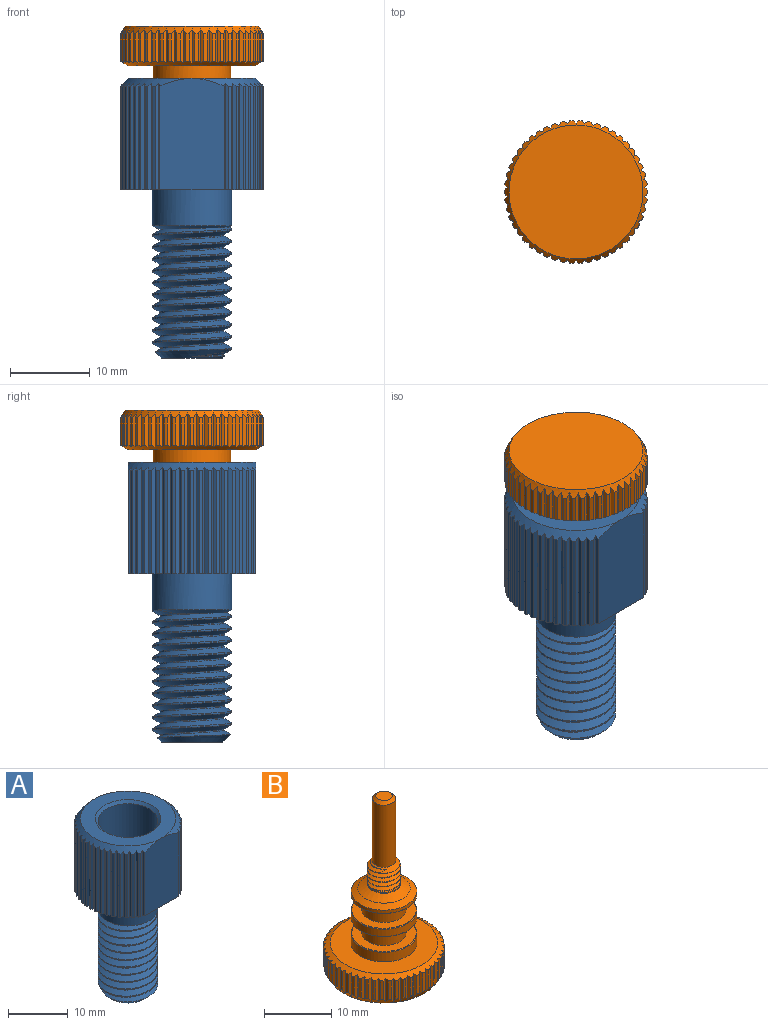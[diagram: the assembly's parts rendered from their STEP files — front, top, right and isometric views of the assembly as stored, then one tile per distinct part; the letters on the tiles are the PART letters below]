
ASSEMBLY  parts=2 mates=1
PART A: 163 faces, bbox 18.3x18.3x36.1 mm
  f0: plane 6.91x6.91mm, normal (0,0,-1), area 7.4mm2, adj f68,f74,f159,f160,f161
  f1: cone r=8mm half-angle=45deg, axis (0,0,-1), area 26.7mm2, adj f21,f22,f23,f24,f25,f26,f27,f28
  f2: plane 18x16mm, normal (0,0,-1), area 59.2mm2, adj f4,f5,f6,f7,f8,f9,f10,f11
  f3: plane 10.82x10.82mm, normal (0,0,-1), area 13.4mm2, adj f45,f156
  f4: cylinder r=9mm len=13mm, axis (0,0,-1), area 5.5mm2, adj f2,f79,f150,f153
  f5: cylinder r=9mm len=13mm, axis (0,0,-1), area 5.5mm2, adj f2,f79,f148,f151
  f6: cylinder r=9mm len=13mm, axis (0,0,-1), area 5.5mm2, adj f2,f79,f146,f149
  f7: cylinder r=9mm len=13mm, axis (0,0,-1), area 5.5mm2, adj f2,f79,f144,f147
  f8: cylinder r=9mm len=13mm, axis (0,0,-1), area 5.5mm2, adj f2,f79,f142,f145
  f9: cylinder r=9mm len=13mm, axis (0,0,-1), area 5.5mm2, adj f2,f79,f140,f143
  f10: cylinder r=9mm len=13mm, axis (0,0,-1), area 5.5mm2, adj f2,f79,f138,f141
  f11: cylinder r=9mm len=13mm, axis (0,0,-1), area 5.5mm2, adj f2,f79,f136,f139
  f12: cylinder r=9mm len=13mm, axis (0,0,-1), area 5.5mm2, adj f2,f79,f134,f137
  f13: cylinder r=9mm len=13mm, axis (0,0,-1), area 5.5mm2, adj f2,f79,f132,f135
  f14: cylinder r=9mm len=13mm, axis (0,0,-1), area 5.5mm2, adj f2,f79,f130,f133
  f15: cylinder r=9mm len=13mm, axis (0,0,-1), area 5.5mm2, adj f2,f79,f128,f131
  f16: cylinder r=9mm len=13mm, axis (0,0,-1), area 5.5mm2, adj f2,f79,f126,f129
  f17: cylinder r=9mm len=13mm, axis (0,0,-1), area 5.5mm2, adj f2,f79,f124,f127
  f18: cylinder r=9mm len=13mm, axis (0,0,-1), area 5.5mm2, adj f2,f79,f122,f125
  f19: cylinder r=9mm len=13mm, axis (0,0,-1), area 5.5mm2, adj f2,f79,f120,f123
  f20: cylinder r=9mm len=13mm, axis (0,0,-1), area 5.5mm2, adj f2,f79,f118,f121
  f21: cylinder r=9mm len=13mm, axis (0,0,-1), area 5.5mm2, adj f1,f2,f114,f117
  f22: cylinder r=9mm len=13mm, axis (0,0,-1), area 5.5mm2, adj f1,f2,f112,f115
  f23: cylinder r=9mm len=13mm, axis (0,0,-1), area 5.5mm2, adj f1,f2,f110,f113
  f24: cylinder r=9mm len=13mm, axis (0,0,-1), area 5.5mm2, adj f1,f2,f108,f111
  f25: cylinder r=9mm len=13mm, axis (0,0,-1), area 5.5mm2, adj f1,f2,f106,f109
  f26: cylinder r=9mm len=13mm, axis (0,0,-1), area 5.5mm2, adj f1,f2,f104,f107
  f27: cylinder r=9mm len=13mm, axis (0,0,-1), area 5.5mm2, adj f1,f2,f102,f105
  f28: cylinder r=9mm len=13mm, axis (0,0,-1), area 5.5mm2, adj f1,f2,f100,f103
  f29: cylinder r=9mm len=13mm, axis (0,0,-1), area 5.5mm2, adj f1,f2,f98,f101
  f30: cylinder r=9mm len=13mm, axis (0,0,-1), area 5.5mm2, adj f1,f2,f96,f99
  f31: cylinder r=9mm len=13mm, axis (0,0,-1), area 5.5mm2, adj f1,f2,f94,f97
  f32: cylinder r=9mm len=13mm, axis (0,0,-1), area 5.5mm2, adj f1,f2,f92,f95
  f33: cylinder r=9mm len=13mm, axis (0,0,-1), area 5.5mm2, adj f1,f2,f90,f93
  f34: cylinder r=9mm len=13mm, axis (0,0,-1), area 5.5mm2, adj f1,f2,f88,f91
  f35: cylinder r=9mm len=13mm, axis (0,0,-1), area 5.5mm2, adj f1,f2,f86,f89
  f36: cylinder r=9mm len=13mm, axis (0,0,-1), area 5.5mm2, adj f1,f2,f84,f87
  f37: cylinder r=9mm len=13mm, axis (0,0,-1), area 5.5mm2, adj f1,f2,f82,f85
  f38: plane 7.75x7.75mm, normal (0,0,-1), area 1.8mm2, adj f41,f80
  f39: cylinder r=4.03mm len=16mm, axis (0,0,-1), area 44.6mm2, adj f40,f41,f43,f44
  f40: bspline ~16.56x11.55mm, area 335.4mm2, adj f39,f41,f42,f44,f45,f46,f47,f48
  f41: cone r=5mm half-angle=45deg, axis (0,0,1), area 24.3mm2, adj f38,f39,f40,f42,f43,f56
  f42: cone r=5mm half-angle=45deg, axis (0,0,1), area 0mm2, adj f40,f41,f55
  f43: bspline ~17.81x11.55mm, area 323.6mm2, adj f39,f41,f44,f45,f46,f47,f48,f49
  f44: cone r=4.03mm half-angle=65deg, axis (0,0,1), area 15.6mm2, adj f39,f40,f43,f45
  f45: cylinder r=5mm len=10mm, axis (0,0,1), area 144.5mm2, adj f3,f40,f43,f44,f46
  f46: cylinder r=5mm len=10mm, axis (0,0,1), area 5.9mm2, adj f40,f43,f45,f47
  f47: cylinder r=5mm len=10mm, axis (0,0,1), area 5.9mm2, adj f40,f43,f46,f48
  f48: cylinder r=5mm len=10mm, axis (0,0,1), area 5.9mm2, adj f40,f43,f47,f49
  f49: cylinder r=5mm len=10mm, axis (0,0,1), area 5.9mm2, adj f40,f43,f48,f50
  f50: cylinder r=5mm len=10mm, axis (0,0,1), area 5.9mm2, adj f40,f43,f49,f51
  f51: cylinder r=5mm len=10mm, axis (0,0,1), area 5.9mm2, adj f40,f43,f50,f52
  f52: cylinder r=5mm len=10mm, axis (0,0,1), area 5.9mm2, adj f40,f43,f51,f53
  f53: cylinder r=5mm len=10mm, axis (0,0,1), area 5.9mm2, adj f40,f43,f52,f54
  f54: cylinder r=5mm len=10mm, axis (0,0,1), area 5.9mm2, adj f40,f43,f53,f55
  f55: cylinder r=5mm len=10mm, axis (0,0,1), area 5.9mm2, adj f40,f42,f43,f54,f56
  f56: cylinder r=5mm len=2.97mm, axis (0,0,1), area 0.2mm2, adj f41,f43,f55
  f57: plane 16x16mm, normal (0,0,1), area 106mm2, adj f1,f79,f81
  f58: cylinder r=5mm len=11.25mm, axis (0,0,1), area 353.4mm2, adj f59,f81
  f59: plane 10.19x10.19mm, normal (0,0,1), area 62.3mm2, adj f58,f66,f76,f77,f78
  f60: cylinder r=2.1mm len=7.22mm, axis (0,0,1), area 90mm2, adj f61,f67,f75,f76
  f61: cylinder r=2.1mm len=4.2mm, axis (0,0,1), area 3.1mm2, adj f60,f62,f76,f77
  f62: cylinder r=2.1mm len=4.2mm, axis (0,0,1), area 3.1mm2, adj f61,f63,f76,f77
  f63: cylinder r=2.1mm len=4.2mm, axis (0,0,1), area 3.1mm2, adj f62,f64,f76,f77
  f64: cylinder r=2.1mm len=4.2mm, axis (0,0,1), area 3.1mm2, adj f63,f65,f76,f77
  f65: cylinder r=2.1mm len=4.2mm, axis (0,0,1), area 3.1mm2, adj f64,f66,f76,f77
  f66: cylinder r=2.1mm len=4.2mm, axis (0,0,1), area 1.2mm2, adj f59,f65,f76,f77
  f67: plane 5.32x5.32mm, normal (0,0,-1), area 8.4mm2, adj f60,f73
  f68: cylinder r=2.66mm len=5.32mm, axis (0,0,1), area 0.9mm2, adj f0,f69,f159,f160
  f69: cylinder r=2.66mm len=5.32mm, axis (0,0,1), area 1.7mm2, adj f68,f70,f159,f160
  f70: cylinder r=2.66mm len=5.32mm, axis (0,0,1), area 1.7mm2, adj f69,f71,f159,f160
  f71: cylinder r=2.66mm len=5.32mm, axis (0,0,1), area 1.7mm2, adj f70,f72,f159,f160
  f72: cylinder r=2.66mm len=5.32mm, axis (0,0,1), area 1.7mm2, adj f71,f73,f159,f160
  f73: cylinder r=2.66mm len=5.93mm, axis (0,0,1), area 90.5mm2, adj f67,f72,f159,f160,f162
  f74: cylinder r=3.3mm len=6.6mm, axis (0,0,1), area 41.5mm2, adj f0,f80
  f75: plane 0.56x0.4mm, normal (0,1,0), area 0.1mm2, adj f60,f76,f77,f78
  f76: bspline ~5.25x5mm, area 42.5mm2, adj f59,f60,f61,f62,f63,f64,f65,f66
  f77: bspline ~5x5mm, area 39.6mm2, adj f59,f61,f62,f63,f64,f65,f66,f75
  f78: cylinder r=2.5mm len=5mm, axis (0,0,-1), area 8.1mm2, adj f59,f75,f76,f77
  f79: cone r=8mm half-angle=45deg, axis (0,0,-1), area 26.7mm2, adj f4,f5,f6,f7,f8,f9,f10,f11
  f80: cone r=3.8mm half-angle=45deg, axis (0,0,-1), area 15.8mm2, adj f38,f74
  f81: cone r=5mm half-angle=45deg, axis (0,0,1), area 23.3mm2, adj f57,f58
  f82: plane 13.37x0.49mm, normal (-0.28,0.96,0), area 6.6mm2, adj f1,f2,f37,f83
  f83: plane 13.37x0.44mm, normal (0.96,0.28,0), area 5.9mm2, adj f1,f2,f82,f157
  f84: plane 13.37x0.5mm, normal (-0.16,0.99,0), area 6.6mm2, adj f1,f2,f36,f85
  f85: plane 13.37x0.5mm, normal (0.99,0.16,0), area 6.6mm2, adj f1,f2,f37,f84
  f86: plane 13.37x0.51mm, normal (-0.03,1,0), area 6.6mm2, adj f1,f2,f35,f87
  f87: plane 13.37x0.51mm, normal (1,0.03,0), area 6.6mm2, adj f1,f2,f36,f86
  f88: plane 13.37x0.51mm, normal (0.09,1,0), area 6.6mm2, adj f1,f2,f34,f89
  f89: plane 13.37x0.51mm, normal (1,-0.09,0), area 6.6mm2, adj f1,f2,f35,f88
  f90: plane 13.37x0.5mm, normal (0.22,0.98,0), area 6.6mm2, adj f1,f2,f33,f91
  f91: plane 13.37x0.5mm, normal (0.98,-0.22,0), area 6.6mm2, adj f1,f2,f34,f90
  f92: plane 13.37x0.48mm, normal (0.34,0.94,0), area 6.6mm2, adj f1,f2,f32,f93
  f93: plane 13.37x0.48mm, normal (0.94,-0.34,0), area 6.6mm2, adj f1,f2,f33,f92
  f94: plane 13.37x0.45mm, normal (0.45,0.89,0), area 6.6mm2, adj f1,f2,f31,f95
  f95: plane 13.37x0.45mm, normal (0.89,-0.45,0), area 6.6mm2, adj f1,f2,f32,f94
  f96: plane 13.37x0.42mm, normal (0.56,0.83,0), area 6.6mm2, adj f1,f2,f30,f97
  f97: plane 13.37x0.42mm, normal (0.83,-0.56,0), area 6.6mm2, adj f1,f2,f31,f96
  f98: plane 13.37x0.38mm, normal (0.66,0.75,0), area 6.6mm2, adj f1,f2,f29,f99
  f99: plane 13.37x0.38mm, normal (0.75,-0.66,0), area 6.6mm2, adj f1,f2,f30,f98
  f100: plane 13.37x0.38mm, normal (0.75,0.66,0), area 6.6mm2, adj f1,f2,f28,f101
  f101: plane 13.37x0.38mm, normal (0.66,-0.75,0), area 6.6mm2, adj f1,f2,f29,f100
  f102: plane 13.37x0.42mm, normal (0.83,0.56,0), area 6.6mm2, adj f1,f2,f27,f103
  f103: plane 13.37x0.42mm, normal (0.56,-0.83,0), area 6.6mm2, adj f1,f2,f28,f102
  f104: plane 13.37x0.45mm, normal (0.89,0.45,0), area 6.6mm2, adj f1,f2,f26,f105
  f105: plane 13.37x0.45mm, normal (0.45,-0.89,0), area 6.6mm2, adj f1,f2,f27,f104
  f106: plane 13.37x0.48mm, normal (0.94,0.34,0), area 6.6mm2, adj f1,f2,f25,f107
  f107: plane 13.37x0.48mm, normal (0.34,-0.94,0), area 6.6mm2, adj f1,f2,f26,f106
  f108: plane 13.37x0.5mm, normal (0.98,0.22,0), area 6.6mm2, adj f1,f2,f24,f109
  f109: plane 13.37x0.5mm, normal (0.22,-0.98,0), area 6.6mm2, adj f1,f2,f25,f108
  f110: plane 13.37x0.51mm, normal (1,0.09,0), area 6.6mm2, adj f1,f2,f23,f111
  f111: plane 13.37x0.51mm, normal (0.09,-1,0), area 6.6mm2, adj f1,f2,f24,f110
  f112: plane 13.37x0.51mm, normal (1,-0.03,0), area 6.6mm2, adj f1,f2,f22,f113
  f113: plane 13.37x0.51mm, normal (-0.03,-1,0), area 6.6mm2, adj f1,f2,f23,f112
  f114: plane 13.37x0.5mm, normal (0.99,-0.16,0), area 6.6mm2, adj f1,f2,f21,f115
  f115: plane 13.37x0.5mm, normal (-0.16,-0.99,0), area 6.6mm2, adj f1,f2,f22,f114
  f116: plane 13.37x0.44mm, normal (0.96,-0.28,0), area 5.9mm2, adj f1,f2,f117,f158
  f117: plane 13.37x0.49mm, normal (-0.28,-0.96,0), area 6.6mm2, adj f1,f2,f21,f116
  f118: plane 13.37x0.49mm, normal (0.28,-0.96,0), area 6.6mm2, adj f2,f20,f79,f119
  f119: plane 13.37x0.44mm, normal (-0.96,-0.28,0), area 5.9mm2, adj f2,f79,f118,f158
  f120: plane 13.37x0.5mm, normal (0.16,-0.99,0), area 6.6mm2, adj f2,f19,f79,f121
  f121: plane 13.37x0.5mm, normal (-0.99,-0.16,0), area 6.6mm2, adj f2,f20,f79,f120
  f122: plane 13.37x0.51mm, normal (0.03,-1,0), area 6.6mm2, adj f2,f18,f79,f123
  f123: plane 13.37x0.51mm, normal (-1,-0.03,0), area 6.6mm2, adj f2,f19,f79,f122
  f124: plane 13.37x0.51mm, normal (-0.09,-1,0), area 6.6mm2, adj f2,f17,f79,f125
  f125: plane 13.37x0.51mm, normal (-1,0.09,0), area 6.6mm2, adj f2,f18,f79,f124
  f126: plane 13.37x0.5mm, normal (-0.22,-0.98,0), area 6.6mm2, adj f2,f16,f79,f127
  f127: plane 13.37x0.5mm, normal (-0.98,0.22,0), area 6.6mm2, adj f2,f17,f79,f126
  f128: plane 13.37x0.48mm, normal (-0.34,-0.94,0), area 6.6mm2, adj f2,f15,f79,f129
  f129: plane 13.37x0.48mm, normal (-0.94,0.34,0), area 6.6mm2, adj f2,f16,f79,f128
  f130: plane 13.37x0.45mm, normal (-0.45,-0.89,0), area 6.6mm2, adj f2,f14,f79,f131
  f131: plane 13.37x0.45mm, normal (-0.89,0.45,0), area 6.6mm2, adj f2,f15,f79,f130
  f132: plane 13.37x0.42mm, normal (-0.56,-0.83,0), area 6.6mm2, adj f2,f13,f79,f133
  f133: plane 13.37x0.42mm, normal (-0.83,0.56,0), area 6.6mm2, adj f2,f14,f79,f132
  f134: plane 13.37x0.38mm, normal (-0.66,-0.75,0), area 6.6mm2, adj f2,f12,f79,f135
  f135: plane 13.37x0.38mm, normal (-0.75,0.66,0), area 6.6mm2, adj f2,f13,f79,f134
  f136: plane 13.37x0.38mm, normal (-0.75,-0.66,0), area 6.6mm2, adj f2,f11,f79,f137
  f137: plane 13.37x0.38mm, normal (-0.66,0.75,0), area 6.6mm2, adj f2,f12,f79,f136
  f138: plane 13.37x0.42mm, normal (-0.83,-0.56,0), area 6.6mm2, adj f2,f10,f79,f139
  f139: plane 13.37x0.42mm, normal (-0.56,0.83,0), area 6.6mm2, adj f2,f11,f79,f138
  f140: plane 13.37x0.45mm, normal (-0.89,-0.45,0), area 6.6mm2, adj f2,f9,f79,f141
  f141: plane 13.37x0.45mm, normal (-0.45,0.89,0), area 6.6mm2, adj f2,f10,f79,f140
  f142: plane 13.37x0.48mm, normal (-0.94,-0.34,0), area 6.6mm2, adj f2,f8,f79,f143
  f143: plane 13.37x0.48mm, normal (-0.34,0.94,0), area 6.6mm2, adj f2,f9,f79,f142
  f144: plane 13.37x0.5mm, normal (-0.98,-0.22,0), area 6.6mm2, adj f2,f7,f79,f145
  f145: plane 13.37x0.5mm, normal (-0.22,0.98,0), area 6.6mm2, adj f2,f8,f79,f144
  f146: plane 13.37x0.51mm, normal (-1,-0.09,0), area 6.6mm2, adj f2,f6,f79,f147
  f147: plane 13.37x0.51mm, normal (-0.09,1,0), area 6.6mm2, adj f2,f7,f79,f146
  f148: plane 13.37x0.51mm, normal (-1,0.03,0), area 6.6mm2, adj f2,f5,f79,f149
  f149: plane 13.37x0.51mm, normal (0.03,1,0), area 6.6mm2, adj f2,f6,f79,f148
  f150: plane 13.37x0.5mm, normal (-0.99,0.16,0), area 6.6mm2, adj f2,f4,f79,f151
  f151: plane 13.37x0.5mm, normal (0.16,0.99,0), area 6.6mm2, adj f2,f5,f79,f150
  f152: plane 13.37x0.44mm, normal (-0.96,0.28,0), area 5.9mm2, adj f2,f79,f153,f157
  f153: plane 13.37x0.49mm, normal (0.28,0.96,0), area 6.6mm2, adj f2,f4,f79,f152
  f154: cylinder r=7.56mm len=15.12mm, axis (0,0,1), area 59.4mm2, adj f2,f155
  f155: plane 15.12x15.12mm, normal (0,0,-1), area 87.6mm2, adj f154,f156
  f156: cylinder r=5.41mm len=10.82mm, axis (0,0,1), area 42.5mm2, adj f3,f155
  f157: plane 14.01x8.08mm, normal (0,1,0), area 110.4mm2, adj f1,f2,f79,f83,f152
  f158: plane 14.01x8.08mm, normal (0,-1,0), area 110.4mm2, adj f1,f2,f79,f116,f119
  f159: bspline ~6.35x6.35mm, area 54.6mm2, adj f0,f68,f69,f70,f71,f72,f73,f161
  f160: bspline ~6.35x6.35mm, area 59.8mm2, adj f0,f68,f69,f70,f71,f72,f73,f161
  f161: bspline ~6.51x6.35mm, area 10.4mm2, adj f0,f159,f160,f162
  f162: plane 0.69x0.45mm, normal (0.87,-0.49,0), area 0.2mm2, adj f73,f159,f160,f161
PART B: 183 faces, bbox 18.3x18.3x32.1 mm
  f0: cylinder r=2.5mm len=5mm, axis (0,0,-1), area 3.4mm2, adj f4,f175,f176,f178,f182
  f1: cylinder r=2.5mm len=5mm, axis (0,0,-1), area 1.6mm2, adj f2,f5,f175,f176
  f2: cylinder r=2.5mm len=5mm, axis (0,0,-1), area 1.6mm2, adj f1,f3,f175,f176
  f3: cylinder r=2.5mm len=5mm, axis (0,0,-1), area 1.6mm2, adj f2,f4,f175,f176
  f4: cylinder r=2.5mm len=5mm, axis (0,0,-1), area 1.6mm2, adj f0,f3,f175,f176
  f5: cylinder r=2.5mm len=1.44mm, axis (0,0,-1), area 0.1mm2, adj f1,f175,f177
  f6: cylinder r=9mm len=3.42mm, axis (0,0,-1), area 1.5mm2, adj f67,f68,f74,f173
  f7: cylinder r=9mm len=3.42mm, axis (0,0,-1), area 1.5mm2, adj f67,f68,f171,f172
  f8: cylinder r=9mm len=3.42mm, axis (0,0,-1), area 1.5mm2, adj f67,f68,f169,f170
  f9: cylinder r=9mm len=3.42mm, axis (0,0,-1), area 1.5mm2, adj f67,f68,f167,f168
  f10: cylinder r=9mm len=3.42mm, axis (0,0,-1), area 1.5mm2, adj f67,f68,f165,f166
  f11: cylinder r=9mm len=3.42mm, axis (0,0,-1), area 1.5mm2, adj f67,f68,f163,f164
  f12: cylinder r=9mm len=3.42mm, axis (0,0,-1), area 1.5mm2, adj f67,f68,f161,f162
  f13: cylinder r=9mm len=3.42mm, axis (0,0,-1), area 1.5mm2, adj f67,f68,f159,f160
  f14: cylinder r=9mm len=3.42mm, axis (0,0,-1), area 1.5mm2, adj f67,f68,f157,f158
  f15: cylinder r=9mm len=3.42mm, axis (0,0,-1), area 1.5mm2, adj f67,f68,f155,f156
  f16: cylinder r=9mm len=3.42mm, axis (0,0,-1), area 1.5mm2, adj f67,f68,f153,f154
  f17: cylinder r=9mm len=3.42mm, axis (0,0,-1), area 1.5mm2, adj f67,f68,f151,f152
  f18: cylinder r=9mm len=3.42mm, axis (0,0,-1), area 1.5mm2, adj f67,f68,f149,f150
  f19: cylinder r=9mm len=3.42mm, axis (0,0,-1), area 1.5mm2, adj f67,f68,f147,f148
  f20: cylinder r=9mm len=3.42mm, axis (0,0,-1), area 1.5mm2, adj f67,f68,f145,f146
  f21: cylinder r=9mm len=3.42mm, axis (0,0,-1), area 1.5mm2, adj f67,f68,f143,f144
  f22: cylinder r=9mm len=3.42mm, axis (0,0,-1), area 1.5mm2, adj f67,f68,f141,f142
  f23: cylinder r=9mm len=3.42mm, axis (0,0,-1), area 1.5mm2, adj f67,f68,f139,f140
  f24: cylinder r=9mm len=3.42mm, axis (0,0,-1), area 1.5mm2, adj f67,f68,f137,f138
  f25: cylinder r=9mm len=3.42mm, axis (0,0,-1), area 1.5mm2, adj f67,f68,f135,f136
  f26: cylinder r=9mm len=3.42mm, axis (0,0,-1), area 1.5mm2, adj f67,f68,f133,f134
  f27: cylinder r=9mm len=3.42mm, axis (0,0,-1), area 1.5mm2, adj f67,f68,f131,f132
  f28: cylinder r=9mm len=3.42mm, axis (0,0,-1), area 1.5mm2, adj f67,f68,f129,f130
  f29: cylinder r=9mm len=3.42mm, axis (0,0,-1), area 1.5mm2, adj f67,f68,f127,f128
  f30: cylinder r=9mm len=3.42mm, axis (0,0,-1), area 1.5mm2, adj f67,f68,f125,f126
  f31: cylinder r=9mm len=3.42mm, axis (0,0,-1), area 1.5mm2, adj f67,f68,f123,f124
  f32: cylinder r=9mm len=3.42mm, axis (0,0,-1), area 1.5mm2, adj f67,f68,f121,f122
  f33: cylinder r=9mm len=3.42mm, axis (0,0,-1), area 1.5mm2, adj f67,f68,f119,f120
  f34: cylinder r=9mm len=3.42mm, axis (0,0,-1), area 1.5mm2, adj f67,f68,f117,f118
  f35: cylinder r=9mm len=3.42mm, axis (0,0,-1), area 1.5mm2, adj f67,f68,f115,f116
  f36: cylinder r=9mm len=3.42mm, axis (0,0,-1), area 1.5mm2, adj f67,f68,f113,f114
  f37: cylinder r=9mm len=3.42mm, axis (0,0,-1), area 1.5mm2, adj f67,f68,f111,f112
  f38: cylinder r=9mm len=3.42mm, axis (0,0,-1), area 1.5mm2, adj f67,f68,f109,f110
  f39: cylinder r=9mm len=3.42mm, axis (0,0,-1), area 1.5mm2, adj f67,f68,f107,f108
  f40: cylinder r=9mm len=3.42mm, axis (0,0,-1), area 1.5mm2, adj f67,f68,f105,f106
  f41: cylinder r=9mm len=3.42mm, axis (0,0,-1), area 1.5mm2, adj f67,f68,f103,f104
  f42: cylinder r=9mm len=3.42mm, axis (0,0,-1), area 1.5mm2, adj f67,f68,f101,f102
  f43: cylinder r=9mm len=3.42mm, axis (0,0,-1), area 1.5mm2, adj f67,f68,f99,f100
  f44: cylinder r=9mm len=3.42mm, axis (0,0,-1), area 1.5mm2, adj f67,f68,f97,f98
  f45: cylinder r=9mm len=3.42mm, axis (0,0,-1), area 1.5mm2, adj f67,f68,f95,f96
  f46: cylinder r=9mm len=3.42mm, axis (0,0,-1), area 1.5mm2, adj f67,f68,f93,f94
  f47: cylinder r=9mm len=3.42mm, axis (0,0,-1), area 1.5mm2, adj f67,f68,f91,f92
  f48: cylinder r=9mm len=3.42mm, axis (0,0,-1), area 1.5mm2, adj f67,f68,f89,f90
  f49: cylinder r=9mm len=3.42mm, axis (0,0,-1), area 1.5mm2, adj f67,f68,f87,f88
  f50: cylinder r=9mm len=3.42mm, axis (0,0,-1), area 1.5mm2, adj f67,f68,f85,f86
  f51: cylinder r=9mm len=3.42mm, axis (0,0,-1), area 1.5mm2, adj f67,f68,f83,f84
  f52: cylinder r=9mm len=3.42mm, axis (0,0,-1), area 1.5mm2, adj f67,f68,f81,f82
  f53: cylinder r=9mm len=3.42mm, axis (0,0,-1), area 1.5mm2, adj f67,f68,f79,f80
  f54: cylinder r=9mm len=3.42mm, axis (0,0,-1), area 1.5mm2, adj f67,f68,f77,f78
  f55: cylinder r=4.9mm len=9.8mm, axis (0,0,-1), area 17.6mm2, adj f69,f73
  f56: plane 9.6x9.6mm, normal (0,0,-1), area 38.2mm2, adj f57,f73
  f57: cylinder r=3.3mm len=6.6mm, axis (0,0,-1), area 56mm2, adj f56,f58
  f58: plane 9.6x9.6mm, normal (0,0,1), area 38.2mm2, adj f57,f72
  f59: cylinder r=4.9mm len=9.8mm, axis (0,0,-1), area 40mm2, adj f71,f72
  f60: plane 9.6x9.6mm, normal (0,0,-1), area 38.2mm2, adj f61,f71
  f61: cylinder r=3.3mm len=6.6mm, axis (0,0,-1), area 56mm2, adj f60,f62
  f62: plane 9.6x9.6mm, normal (0,0,1), area 38.2mm2, adj f61,f70
  f63: cylinder r=4.9mm len=9.8mm, axis (0,0,-1), area 53.9mm2, adj f64,f70
  f64: plane 16x16mm, normal (0,0,1), area 125.6mm2, adj f63,f68
  f65: cylinder r=9mm len=3.42mm, axis (0,0,-1), area 1.5mm2, adj f67,f68,f75,f76
  f66: plane 16.85x16.85mm, normal (0,0,-1), area 222.9mm2, adj f67
  f67: cone r=8.42mm half-angle=30deg, axis (0,0,1), area 50.6mm2, adj f6,f7,f8,f9,f10,f11,f12,f13
  f68: cone r=9mm half-angle=60deg, axis (0,0,-1), area 54.4mm2, adj f6,f7,f8,f9,f10,f11,f12,f13
  f69: cone r=4.9mm half-angle=60deg, axis (0,0,-1), area 31.9mm2, adj f55,f182
  f70: cone r=4.9mm half-angle=45deg, axis (0,0,-1), area 4.3mm2, adj f62,f63
  f71: cone r=4.8mm half-angle=45deg, axis (0,0,1), area 4.3mm2, adj f59,f60
  f72: cone r=4.9mm half-angle=45deg, axis (0,0,-1), area 4.3mm2, adj f58,f59
  f73: cone r=4.8mm half-angle=45deg, axis (0,0,1), area 4.3mm2, adj f55,f56
  f74: plane 4.26x0.36mm, normal (0.71,0.71,0), area 1.9mm2, adj f6,f67,f68,f75
  f75: plane 4.26x0.36mm, normal (-0.71,0.71,0), area 1.9mm2, adj f65,f67,f68,f74
  f76: plane 4.26x0.4mm, normal (0.79,0.61,0), area 1.9mm2, adj f65,f67,f68,f77
  f77: plane 4.26x0.4mm, normal (-0.61,0.79,0), area 1.9mm2, adj f54,f67,f68,f76
  f78: plane 4.26x0.44mm, normal (0.86,0.51,0), area 1.9mm2, adj f54,f67,f68,f79
  f79: plane 4.26x0.44mm, normal (-0.51,0.86,0), area 1.9mm2, adj f53,f67,f68,f78
  f80: plane 4.26x0.47mm, normal (0.92,0.4,0), area 1.9mm2, adj f53,f67,f68,f81
  f81: plane 4.26x0.47mm, normal (-0.4,0.92,0), area 1.9mm2, adj f52,f67,f68,f80
  f82: plane 4.26x0.49mm, normal (0.96,0.28,0), area 1.9mm2, adj f52,f67,f68,f83
  f83: plane 4.26x0.49mm, normal (-0.28,0.96,0), area 1.9mm2, adj f51,f67,f68,f82
  f84: plane 4.26x0.5mm, normal (0.99,0.16,0), area 1.9mm2, adj f51,f67,f68,f85
  f85: plane 4.26x0.5mm, normal (-0.16,0.99,0), area 1.9mm2, adj f50,f67,f68,f84
  f86: plane 4.26x0.51mm, normal (1,0.03,0), area 1.9mm2, adj f50,f67,f68,f87
  f87: plane 4.26x0.51mm, normal (-0.03,1,0), area 1.9mm2, adj f49,f67,f68,f86
  f88: plane 4.26x0.51mm, normal (1,-0.09,0), area 1.9mm2, adj f49,f67,f68,f89
  f89: plane 4.26x0.51mm, normal (0.09,1,0), area 1.9mm2, adj f48,f67,f68,f88
  f90: plane 4.26x0.5mm, normal (0.98,-0.22,0), area 1.9mm2, adj f48,f67,f68,f91
  f91: plane 4.26x0.5mm, normal (0.22,0.98,0), area 1.9mm2, adj f47,f67,f68,f90
  f92: plane 4.26x0.48mm, normal (0.94,-0.34,0), area 1.9mm2, adj f47,f67,f68,f93
  f93: plane 4.26x0.48mm, normal (0.34,0.94,0), area 1.9mm2, adj f46,f67,f68,f92
  f94: plane 4.26x0.46mm, normal (0.89,-0.45,0), area 1.9mm2, adj f46,f67,f68,f95
  f95: plane 4.26x0.46mm, normal (0.45,0.89,0), area 1.9mm2, adj f45,f67,f68,f94
  f96: plane 4.26x0.42mm, normal (0.83,-0.56,0), area 1.9mm2, adj f45,f67,f68,f97
  f97: plane 4.26x0.42mm, normal (0.56,0.83,0), area 1.9mm2, adj f44,f67,f68,f96
  f98: plane 4.26x0.38mm, normal (0.75,-0.66,0), area 1.9mm2, adj f44,f67,f68,f99
  f99: plane 4.26x0.38mm, normal (0.66,0.75,0), area 1.9mm2, adj f43,f67,f68,f98
  f100: plane 4.26x0.38mm, normal (0.66,-0.75,0), area 1.9mm2, adj f43,f67,f68,f101
  f101: plane 4.26x0.38mm, normal (0.75,0.66,0), area 1.9mm2, adj f42,f67,f68,f100
  f102: plane 4.26x0.42mm, normal (0.56,-0.83,0), area 1.9mm2, adj f42,f67,f68,f103
  f103: plane 4.26x0.42mm, normal (0.83,0.56,0), area 1.9mm2, adj f41,f67,f68,f102
  f104: plane 4.26x0.46mm, normal (0.45,-0.89,0), area 1.9mm2, adj f41,f67,f68,f105
  f105: plane 4.26x0.46mm, normal (0.89,0.45,0), area 1.9mm2, adj f40,f67,f68,f104
  f106: plane 4.26x0.48mm, normal (0.34,-0.94,0), area 1.9mm2, adj f40,f67,f68,f107
  f107: plane 4.26x0.48mm, normal (0.94,0.34,0), area 1.9mm2, adj f39,f67,f68,f106
  f108: plane 4.26x0.5mm, normal (0.22,-0.98,0), area 1.9mm2, adj f39,f67,f68,f109
  f109: plane 4.26x0.5mm, normal (0.98,0.22,0), area 1.9mm2, adj f38,f67,f68,f108
  f110: plane 4.26x0.51mm, normal (0.09,-1,0), area 1.9mm2, adj f38,f67,f68,f111
  f111: plane 4.26x0.51mm, normal (1,0.09,0), area 1.9mm2, adj f37,f67,f68,f110
  f112: plane 4.26x0.51mm, normal (-0.03,-1,0), area 1.9mm2, adj f37,f67,f68,f113
  f113: plane 4.26x0.51mm, normal (1,-0.03,0), area 1.9mm2, adj f36,f67,f68,f112
  f114: plane 4.26x0.5mm, normal (-0.16,-0.99,0), area 1.9mm2, adj f36,f67,f68,f115
  f115: plane 4.26x0.5mm, normal (0.99,-0.16,0), area 1.9mm2, adj f35,f67,f68,f114
  f116: plane 4.26x0.49mm, normal (-0.28,-0.96,0), area 1.9mm2, adj f35,f67,f68,f117
  f117: plane 4.26x0.49mm, normal (0.96,-0.28,0), area 1.9mm2, adj f34,f67,f68,f116
  f118: plane 4.26x0.47mm, normal (-0.4,-0.92,0), area 1.9mm2, adj f34,f67,f68,f119
  f119: plane 4.26x0.47mm, normal (0.92,-0.4,0), area 1.9mm2, adj f33,f67,f68,f118
  f120: plane 4.26x0.44mm, normal (-0.51,-0.86,0), area 1.9mm2, adj f33,f67,f68,f121
  f121: plane 4.26x0.44mm, normal (0.86,-0.51,0), area 1.9mm2, adj f32,f67,f68,f120
  f122: plane 4.26x0.4mm, normal (-0.61,-0.79,0), area 1.9mm2, adj f32,f67,f68,f123
  f123: plane 4.26x0.4mm, normal (0.79,-0.61,0), area 1.9mm2, adj f31,f67,f68,f122
  f124: plane 4.26x0.36mm, normal (-0.71,-0.71,0), area 1.9mm2, adj f31,f67,f68,f125
  f125: plane 4.26x0.36mm, normal (0.71,-0.71,0), area 1.9mm2, adj f30,f67,f68,f124
  f126: plane 4.26x0.4mm, normal (-0.79,-0.61,0), area 1.9mm2, adj f30,f67,f68,f127
  f127: plane 4.26x0.4mm, normal (0.61,-0.79,0), area 1.9mm2, adj f29,f67,f68,f126
  f128: plane 4.26x0.44mm, normal (-0.86,-0.51,0), area 1.9mm2, adj f29,f67,f68,f129
  f129: plane 4.26x0.44mm, normal (0.51,-0.86,0), area 1.9mm2, adj f28,f67,f68,f128
  f130: plane 4.26x0.47mm, normal (-0.92,-0.4,0), area 1.9mm2, adj f28,f67,f68,f131
  f131: plane 4.26x0.47mm, normal (0.4,-0.92,0), area 1.9mm2, adj f27,f67,f68,f130
  f132: plane 4.26x0.49mm, normal (-0.96,-0.28,0), area 1.9mm2, adj f27,f67,f68,f133
  f133: plane 4.26x0.49mm, normal (0.28,-0.96,0), area 1.9mm2, adj f26,f67,f68,f132
  f134: plane 4.26x0.5mm, normal (-0.99,-0.16,0), area 1.9mm2, adj f26,f67,f68,f135
  f135: plane 4.26x0.5mm, normal (0.16,-0.99,0), area 1.9mm2, adj f25,f67,f68,f134
  f136: plane 4.26x0.51mm, normal (-1,-0.03,0), area 1.9mm2, adj f25,f67,f68,f137
  f137: plane 4.26x0.51mm, normal (0.03,-1,0), area 1.9mm2, adj f24,f67,f68,f136
  f138: plane 4.26x0.51mm, normal (-1,0.09,0), area 1.9mm2, adj f24,f67,f68,f139
  f139: plane 4.26x0.51mm, normal (-0.09,-1,0), area 1.9mm2, adj f23,f67,f68,f138
  f140: plane 4.26x0.5mm, normal (-0.98,0.22,0), area 1.9mm2, adj f23,f67,f68,f141
  f141: plane 4.26x0.5mm, normal (-0.22,-0.98,0), area 1.9mm2, adj f22,f67,f68,f140
  f142: plane 4.26x0.48mm, normal (-0.94,0.34,0), area 1.9mm2, adj f22,f67,f68,f143
  f143: plane 4.26x0.48mm, normal (-0.34,-0.94,0), area 1.9mm2, adj f21,f67,f68,f142
  f144: plane 4.26x0.46mm, normal (-0.89,0.45,0), area 1.9mm2, adj f21,f67,f68,f145
  f145: plane 4.26x0.46mm, normal (-0.45,-0.89,0), area 1.9mm2, adj f20,f67,f68,f144
  f146: plane 4.26x0.42mm, normal (-0.83,0.56,0), area 1.9mm2, adj f20,f67,f68,f147
  f147: plane 4.26x0.42mm, normal (-0.56,-0.83,0), area 1.9mm2, adj f19,f67,f68,f146
  f148: plane 4.26x0.38mm, normal (-0.75,0.66,0), area 1.9mm2, adj f19,f67,f68,f149
  f149: plane 4.26x0.38mm, normal (-0.66,-0.75,0), area 1.9mm2, adj f18,f67,f68,f148
  f150: plane 4.26x0.38mm, normal (-0.66,0.75,0), area 1.9mm2, adj f18,f67,f68,f151
  f151: plane 4.26x0.38mm, normal (-0.75,-0.66,0), area 1.9mm2, adj f17,f67,f68,f150
  f152: plane 4.26x0.42mm, normal (-0.56,0.83,0), area 1.9mm2, adj f17,f67,f68,f153
  f153: plane 4.26x0.42mm, normal (-0.83,-0.56,0), area 1.9mm2, adj f16,f67,f68,f152
  f154: plane 4.26x0.46mm, normal (-0.45,0.89,0), area 1.9mm2, adj f16,f67,f68,f155
  f155: plane 4.26x0.46mm, normal (-0.89,-0.45,0), area 1.9mm2, adj f15,f67,f68,f154
  f156: plane 4.26x0.48mm, normal (-0.34,0.94,0), area 1.9mm2, adj f15,f67,f68,f157
  f157: plane 4.26x0.48mm, normal (-0.94,-0.34,0), area 1.9mm2, adj f14,f67,f68,f156
  f158: plane 4.26x0.5mm, normal (-0.22,0.98,0), area 1.9mm2, adj f14,f67,f68,f159
  f159: plane 4.26x0.5mm, normal (-0.98,-0.22,0), area 1.9mm2, adj f13,f67,f68,f158
  f160: plane 4.26x0.51mm, normal (-0.09,1,0), area 1.9mm2, adj f13,f67,f68,f161
  f161: plane 4.26x0.51mm, normal (-1,-0.09,0), area 1.9mm2, adj f12,f67,f68,f160
  f162: plane 4.26x0.51mm, normal (0.03,1,0), area 1.9mm2, adj f12,f67,f68,f163
  f163: plane 4.26x0.51mm, normal (-1,0.03,0), area 1.9mm2, adj f11,f67,f68,f162
  f164: plane 4.26x0.5mm, normal (0.16,0.99,0), area 1.9mm2, adj f11,f67,f68,f165
  f165: plane 4.26x0.5mm, normal (-0.99,0.16,0), area 1.9mm2, adj f10,f67,f68,f164
  f166: plane 4.26x0.49mm, normal (0.28,0.96,0), area 1.9mm2, adj f10,f67,f68,f167
  f167: plane 4.26x0.49mm, normal (-0.96,0.28,0), area 1.9mm2, adj f9,f67,f68,f166
  f168: plane 4.26x0.47mm, normal (0.4,0.92,0), area 1.9mm2, adj f9,f67,f68,f169
  f169: plane 4.26x0.47mm, normal (-0.92,0.4,0), area 1.9mm2, adj f8,f67,f68,f168
  f170: plane 4.26x0.44mm, normal (0.51,0.86,0), area 1.9mm2, adj f8,f67,f68,f171
  f171: plane 4.26x0.44mm, normal (-0.86,0.51,0), area 1.9mm2, adj f7,f67,f68,f170
  f172: plane 4.26x0.4mm, normal (0.61,0.79,0), area 1.9mm2, adj f7,f67,f68,f173
  f173: plane 4.26x0.4mm, normal (-0.79,0.61,0), area 1.9mm2, adj f6,f67,f68,f172
  f174: cylinder r=1.98mm len=3.96mm, axis (0,0,1), area 5.9mm2, adj f175,f176,f177,f178
  f175: bspline ~5x5mm, area 38.3mm2, adj f0,f1,f2,f3,f4,f5,f174,f177
  f176: bspline ~5x5mm, area 38.4mm2, adj f0,f1,f2,f3,f4,f174,f177,f178
  f177: cone r=1.73mm half-angle=55deg, axis (0,0,-1), area 7.9mm2, adj f5,f174,f175,f176,f179
  f178: plane 5.31x5.31mm, normal (0,0,1), area 3.8mm2, adj f0,f174,f175,f176
  f179: cylinder r=1.73mm len=11.3mm, axis (0,0,-1), area 122.6mm2, adj f177,f181
  f180: plane 2.45x2.45mm, normal (0,0,1), area 4.7mm2, adj f181
  f181: cone r=1.23mm half-angle=45deg, axis (0,0,-1), area 6.6mm2, adj f179,f180
  f182: cone r=2.5mm half-angle=60deg, axis (0,0,-1), area 32.5mm2, adj f0,f69
PLACE A t=(-0.04,-0.16,3.83)mm
PLACE B rot(axis=(1,0,0),180deg) t=(-0.04,-0.16,9.43)mm
MATE fastened B.f0 <-> A.f1  axis (0,0,-1) through (-0.04,-0.16,8.62)mm
